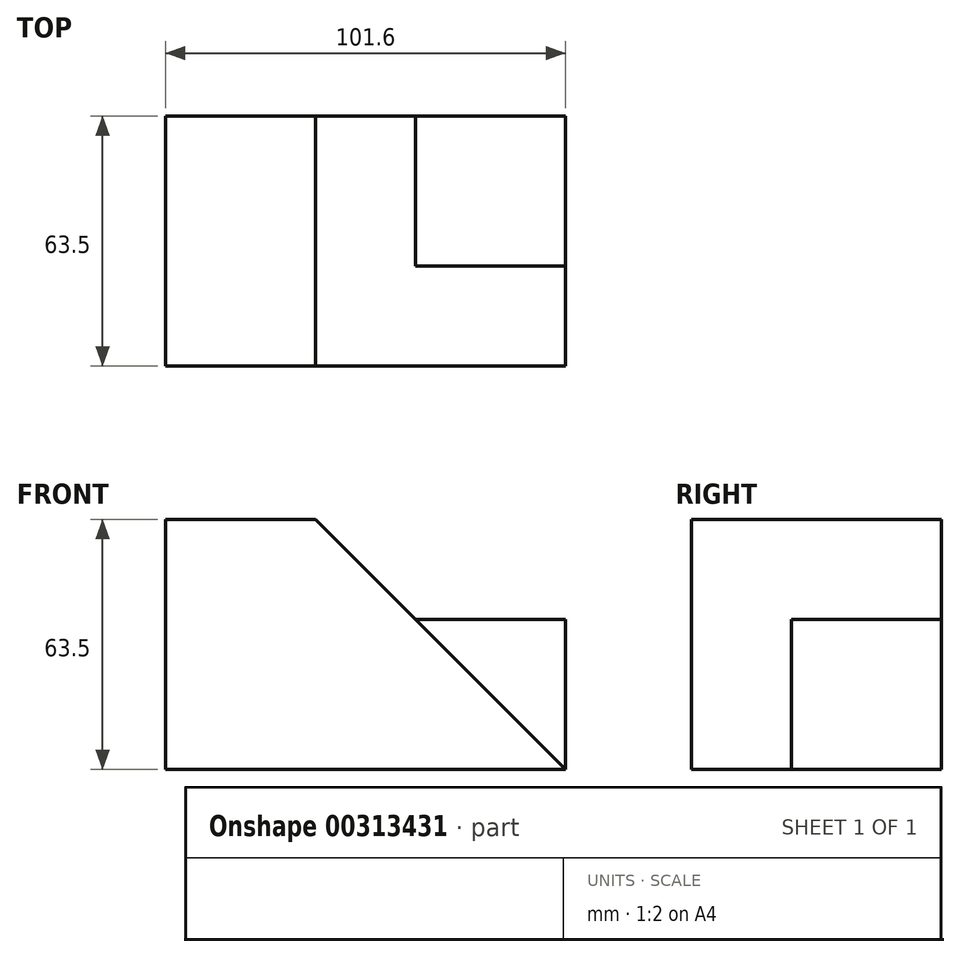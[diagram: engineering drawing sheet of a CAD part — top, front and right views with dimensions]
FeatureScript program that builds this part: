
annotation { "Feature Type Name" : "Feature", "Feature Type Description" : "" }
export const myFeature = defineFeature(function(context is Context, id is Id, definition is map)
    precondition{}
    {
        {
            var Q0;
            Q0=qCreatedBy(makeId("Front.planeOp"),FACE);
            var sketch = newSketch(context, id + "F0", { "sketchPlane" : qUnion([Q0])});
            skLineSegment(sketch, "E0", {"start": v(-50.49, -37.8) * mm, "end": v(51.11, -37.8) * mm});
            skLineSegment(sketch, "E1", {"start": v(-50.49, -37.8) * mm, "end": v(-50.49, 25.7) * mm});
            skLineSegment(sketch, "E2", {"start": v(-50.49, 25.7) * mm, "end": v(-12.39, 25.7) * mm});
            skLineSegment(sketch, "E3", {"start": v(-12.39, 25.7) * mm, "end": v(51.11, -37.8) * mm});
            skSolve(sketch);
        }
        {
            var Q0;
            Q0=makeQuery(id+"F0.imprint","IMPRINT",FACE,{"disambiguationData":[TD([[makeQuery(id+"F0.imprint","IMPRINT",EDGE,{"derivedFrom":sQuery(id+"F0.wireOp",EDGE,"E0")}),1.0]])]});
            extrude(context, id + "F1", {"entities" : qUnion([Q0]), "depth" : 63.5 * mm});
        }
        {
            var Q0;
            Q0=makeQuery(id+"F1.opExtrude","CAP_FACE",FACE,{"disambiguationData":[OSD([sQuery(id+"F0.wireOp",EDGE,"E0"),sQuery(id+"F0.wireOp",EDGE,"E1"),sQuery(id+"F0.wireOp",EDGE,"E2"),sQuery(id+"F0.wireOp",EDGE,"E3")])],"isStart":true});
            var sketch = newSketch(context, id + "F2", { "sketchPlane" : qUnion([Q0])});
            skLineSegment(sketch, "E4", {"start": v(-51.11, -37.8) * mm, "end": v(-51.11, 0.3) * mm});
            skLineSegment(sketch, "E5", {"start": v(-51.11, 0.3) * mm, "end": v(-13.01, 0.3) * mm});
            skLineSegment(sketch, "E6", {"start": v(-13.01, 0.3) * mm, "end": v(-51.11, -37.8) * mm});
            skSolve(sketch);
        }
        {
            var Q0;
            Q0=makeQuery(id+"F2.imprint","IMPRINT",FACE,{"disambiguationData":[TD([[makeQuery(id+"F2.imprint","IMPRINT",EDGE,{"derivedFrom":sQuery(id+"F2.wireOp",EDGE,"E4")}),-1.0]])]});
            extrude(context, id + "F3", {"entities" : qUnion([Q0]), "operationType" : NewBodyOperationType.ADD, "depth" : -38.1 * mm});
        }
    });
